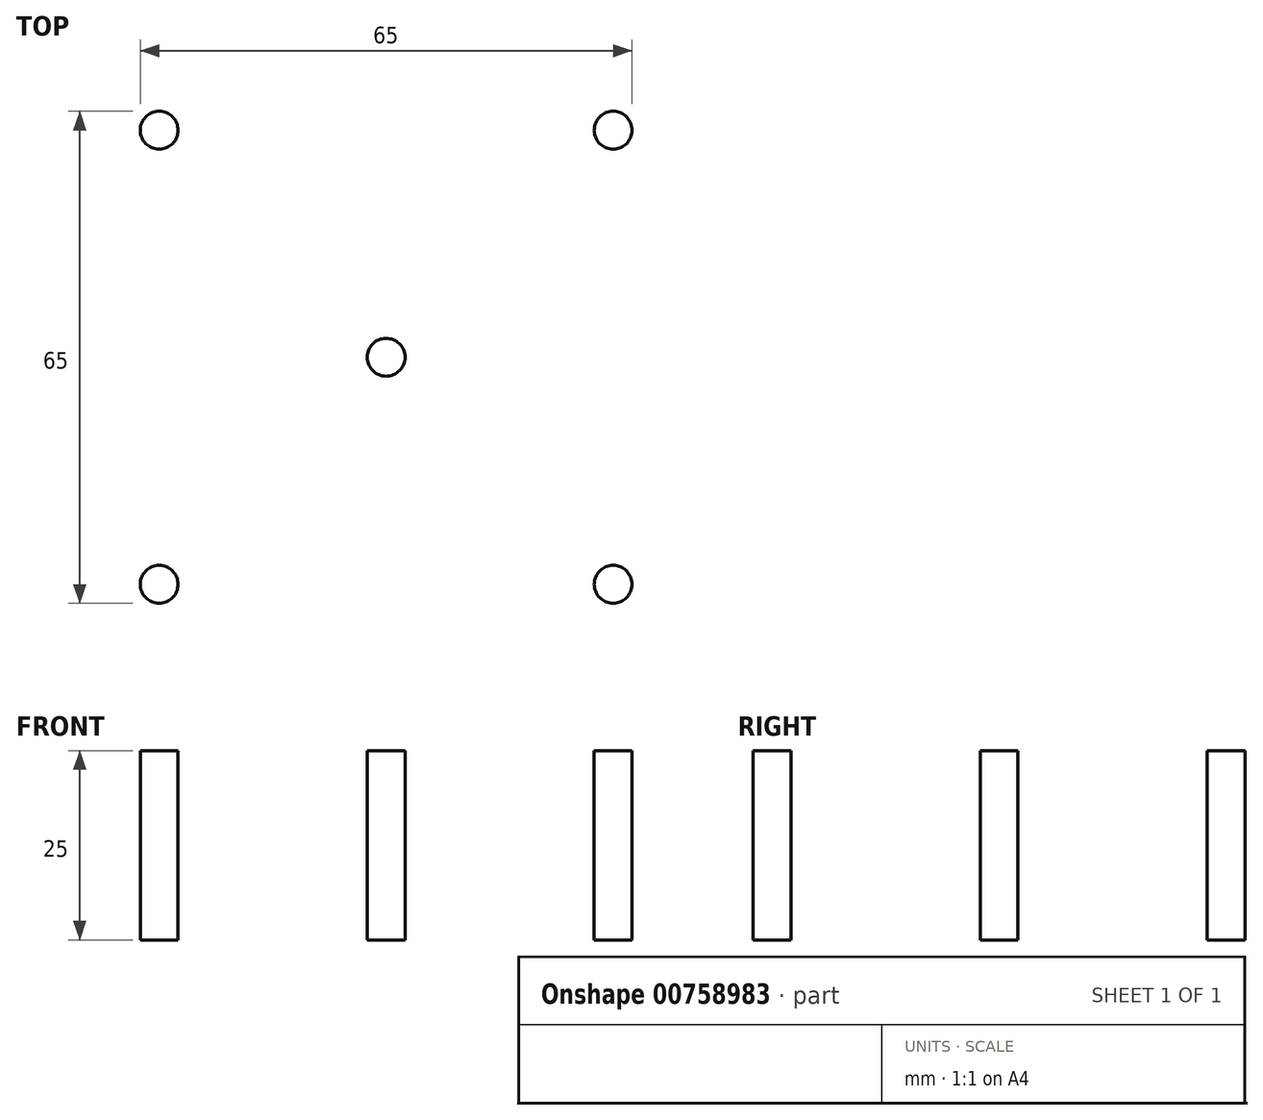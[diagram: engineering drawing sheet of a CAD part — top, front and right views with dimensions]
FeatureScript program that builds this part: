
annotation { "Feature Type Name" : "Feature", "Feature Type Description" : "" }
export const myFeature = defineFeature(function(context is Context, id is Id, definition is map)
    precondition{}
    {
        {
            var Q0;
            Q0=qCreatedBy(makeId("Top.planeOp"),FACE);
            var sketch = newSketch(context, id + "F0", { "sketchPlane" : qUnion([Q0])});
            skCircle(sketch, "E0", {"center": v(0, 0) * mm, "radius": 2.5 * mm});
            skCircle(sketch, "E1", {"center": v(30, 30) * mm, "radius": 2.5 * mm});
            skCircle(sketch, "E2", {"center": v(-30, 30) * mm, "radius": 2.5 * mm});
            skCircle(sketch, "E3", {"center": v(-30, -30) * mm, "radius": 2.5 * mm});
            skCircle(sketch, "E4", {"center": v(30, -30) * mm, "radius": 2.5 * mm});
            skSolve(sketch);
        }
        {
            var Q0;
            Q0 = qSketchRegion(id + "F0", true);
            extrude(context, id + "F1", {"entities" : qUnion([Q0]), "oppositeDirection" : true, "depth" : 25 * mm, "offsetDistance" : 25 * mm});
        }
    });
